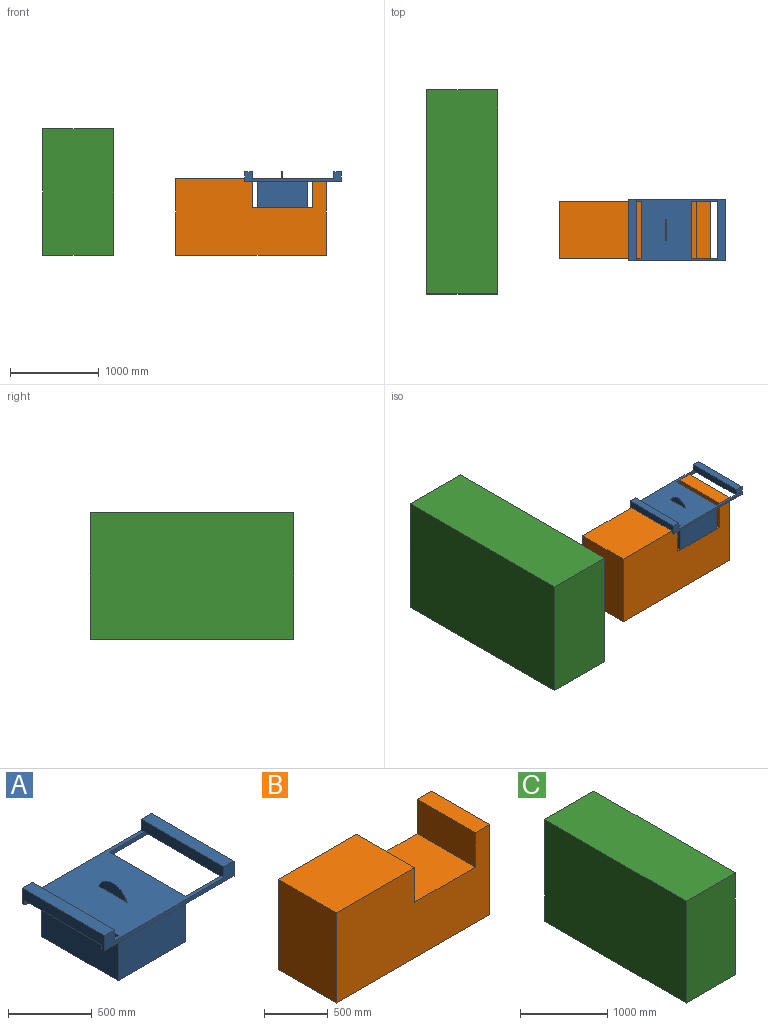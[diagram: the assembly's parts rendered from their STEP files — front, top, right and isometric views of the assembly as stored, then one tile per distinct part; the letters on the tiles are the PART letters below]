
ASSEMBLY  parts=3 mates=1
PART A: 25 faces, bbox 1090x695x410 mm
  f0: plane 920x695mm, normal (0,0,1), area 412950.3mm2, adj f3,f4,f6,f10,f11,f12,f14,f15
  f1: plane 570x300mm, normal (0,1,0), area 171000mm2, adj f3,f4,f5,f13
  f2: plane 570x300mm, normal (0,-1,0), area 171000mm2, adj f3,f4,f5,f8
  f3: plane 645x330mm, normal (-1,0,0), area 212850mm2, adj f0,f1,f2,f5,f6,f15
  f4: plane 645x330mm, normal (1,0,0), area 212850mm2, adj f0,f1,f2,f5,f11,f12
  f5: plane 645x570mm, normal (0,0,-1), area 367650mm2, adj f1,f2,f3,f4
  f6: plane 140x30mm, normal (0,1,0), area 4200mm2, adj f0,f3,f7,f8,f19
  f7: plane 695x110mm, normal (-1,0,0), area 57100mm2, adj f6,f8,f10,f13,f14,f15,f19,f21
  f8: plane 1090x25mm, normal (0,0,-1), area 27250mm2, adj f2,f6,f7,f9,f10,f11
  f9: plane 695x110mm, normal (1,0,0), area 57100mm2, adj f8,f10,f11,f12,f13,f14,f16,f18
  f10: plane 1090x110mm, normal (0,-1,0), area 46300mm2, adj f0,f7,f8,f9,f17,f18,f20,f21
  f11: plane 380x30mm, normal (0,1,0), area 11400mm2, adj f0,f4,f8,f9,f16
  f12: plane 380x30mm, normal (0,-1,0), area 11400mm2, adj f0,f4,f9,f13,f16
  f13: plane 1090x25mm, normal (0,0,-1), area 27250mm2, adj f1,f7,f9,f12,f14,f15
  f14: plane 1090x110mm, normal (0,1,0), area 46300mm2, adj f0,f7,f9,f13,f17,f18,f20,f21
  f15: plane 140x30mm, normal (0,-1,0), area 4200mm2, adj f0,f3,f7,f13,f19
  f16: plane 645x85mm, normal (0,0,-1), area 54825mm2, adj f9,f11,f12,f17
  f17: plane 695x80mm, normal (-1,0,0), area 55600mm2, adj f0,f10,f14,f16,f18
  f18: plane 695x85mm, normal (0,0,1), area 59075mm2, adj f9,f10,f14,f17
  f19: plane 645x85mm, normal (0,0,-1), area 54825mm2, adj f6,f7,f15,f20
  f20: plane 695x80mm, normal (1,0,0), area 55600mm2, adj f0,f10,f14,f19,f21
  f21: plane 695x85mm, normal (0,0,1), area 59075mm2, adj f7,f10,f14,f20
  f22: cylinder r=125mm len=233.24mm, axis (1,0,0), area 901.9mm2, adj f0,f23,f24
  f23: plane 233.24x80mm, normal (-1,0,0), area 13541.7mm2, adj f0,f22
  f24: plane 233.24x80mm, normal (1,0,0), area 13541.7mm2, adj f0,f22
PART B: 10 faces, bbox 1700x645x865 mm
  f0: plane 1700x865mm, normal (0,-1,0), area 1249400mm2, adj f1,f2,f3,f4,f5,f6,f7,f8
  f1: plane 1700x645mm, normal (0,0,-1), area 1096500mm2, adj f0,f2,f6,f9
  f2: plane 865x645mm, normal (1,0,0), area 557925mm2, adj f0,f1,f3,f9
  f3: plane 645x160mm, normal (0,0,1), area 103200mm2, adj f0,f2,f4,f9
  f4: plane 645x330mm, normal (-1,0,0), area 212850mm2, adj f0,f3,f5,f9
  f5: plane 670x645mm, normal (0,0,1), area 432150mm2, adj f0,f4,f7,f9
  f6: plane 865x645mm, normal (-1,0,0), area 557925mm2, adj f0,f1,f8,f9
  f7: plane 645x330mm, normal (1,0,0), area 212850mm2, adj f0,f5,f8,f9
  f8: plane 870x645mm, normal (0,0,1), area 561150mm2, adj f0,f6,f7,f9
  f9: plane 1700x865mm, normal (0,1,0), area 1249400mm2, adj f1,f2,f3,f4,f5,f6,f7,f8
PART C: 6 faces, bbox 800x2300x1430 mm
  f0: plane 2300x800mm, normal (0,0,-1), area 1840000mm2, adj f1,f3,f4,f5
  f1: plane 1430x800mm, normal (0,1,0), area 1144000mm2, adj f0,f2,f4,f5
  f2: plane 2300x800mm, normal (0,0,1), area 1840000mm2, adj f1,f3,f4,f5
  f3: plane 1430x800mm, normal (0,-1,0), area 1144000mm2, adj f0,f2,f4,f5
  f4: plane 2300x1430mm, normal (1,0,0), area 3289000mm2, adj f0,f1,f2,f3
  f5: plane 2300x1430mm, normal (-1,0,0), area 3289000mm2, adj f0,f1,f2,f3
PLACE A t=(-5,0,0)mm
PLACE B t=(-5,0,0)mm
PLACE C rot(axis=(-0.67,0,0.74),0deg) t=(-2305,1577.5,-535)mm
MATE fastened B.f5 <-> A.f5  axis (0,0,1) through (0,0,0)mm
